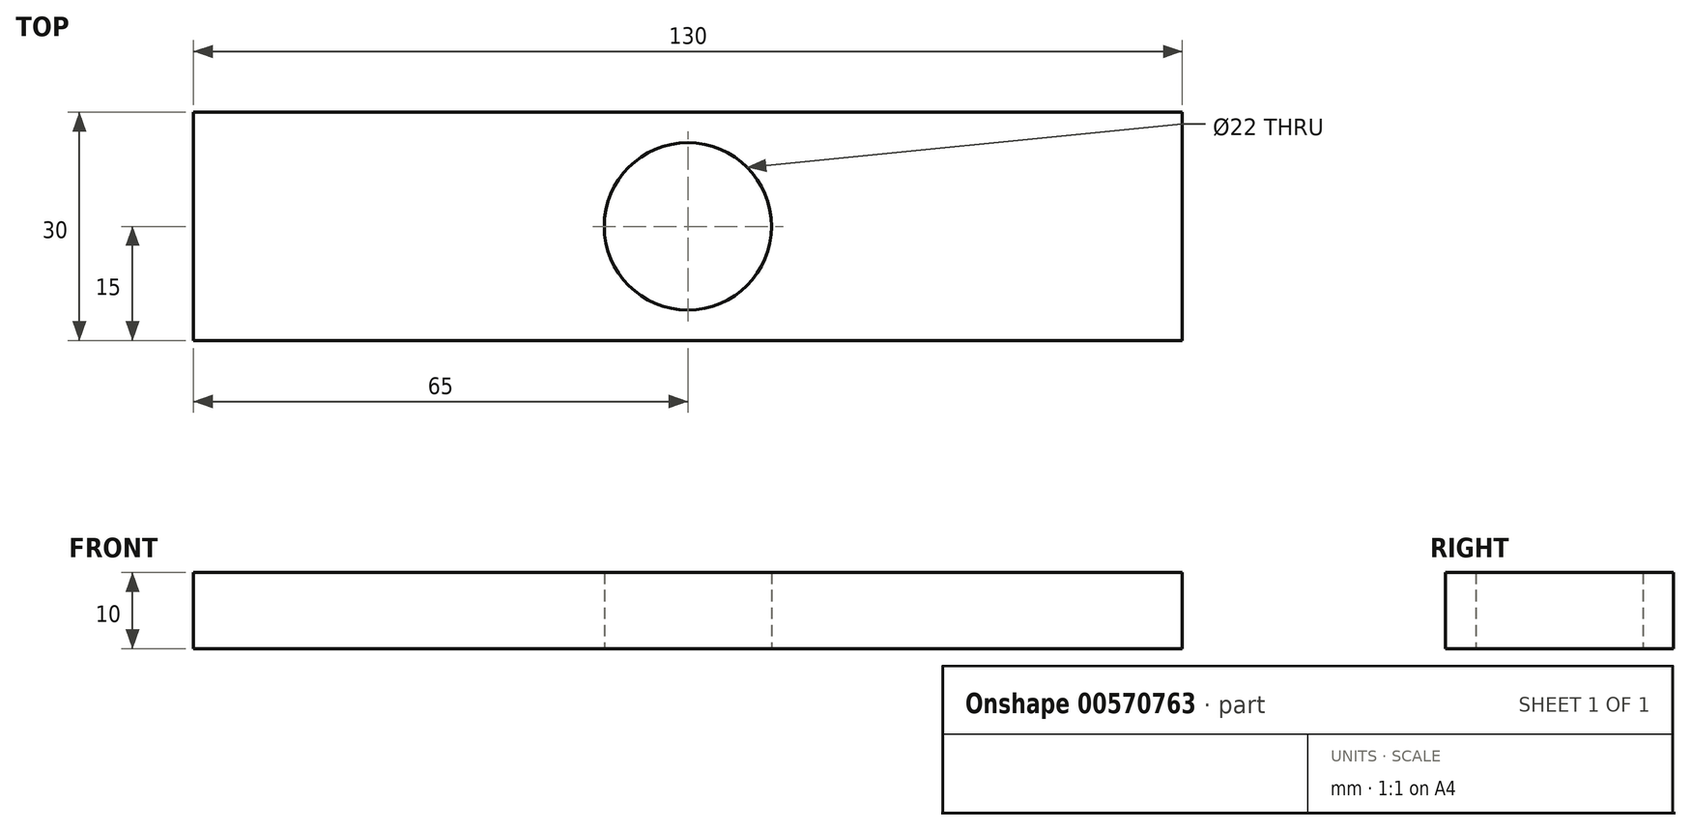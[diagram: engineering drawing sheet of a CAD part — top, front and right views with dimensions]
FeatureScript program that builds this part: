
annotation { "Feature Type Name" : "Feature", "Feature Type Description" : "" }
export const myFeature = defineFeature(function(context is Context, id is Id, definition is map)
    precondition{}
    {
        {
            var Q0;
            Q0=qCreatedBy(makeId("Top.planeOp"),FACE);
            var sketch = newSketch(context, id + "F0", { "sketchPlane" : qUnion([Q0])});
            skCircle(sketch, "E0", {"center": v(0, 0) * mm, "radius": 11 * mm});
            skLineSegment(sketch, "E1.bottom", {"start": v(65, 15) * mm, "end": v(-65, 15) * mm});
            skLineSegment(sketch, "E1.top", {"start": v(65, -15) * mm, "end": v(-65, -15) * mm});
            skLineSegment(sketch, "E1.left", {"start": v(65, 15) * mm, "end": v(65, -15) * mm});
            skLineSegment(sketch, "E1.right", {"start": v(-65, 15) * mm, "end": v(-65, -15) * mm});
            skSolve(sketch);
        }
        {
            var Q0;
            Q0 = qSketchRegion(id + "F0", true);
            extrude(context, id + "F1", {"entities" : qUnion([Q0]), "depth" : 10 * mm, "offsetDistance" : 25 * mm});
        }
    });
